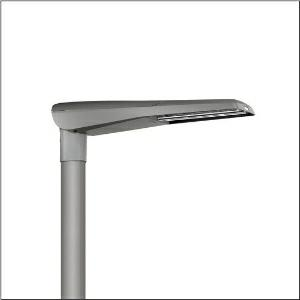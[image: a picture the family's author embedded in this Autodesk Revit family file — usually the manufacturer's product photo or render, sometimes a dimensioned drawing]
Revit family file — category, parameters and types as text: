
# Revit family: streetlight_sl_11_iq_mini___st0_5st0_5_5xc2hc1f08he_bd04
name_source: partatom
category: Lighting Fixtures
units: mm (PartAtom-declared; Revit-internal decimal feet)

## family parameters
Cut with Voids When Loaded = No
Host = Face
Light Source = No
Part Type = Normal
Room Calculation Point = No
Round Connector Dimension = Use Diameter
Shared = No

## types (1)
- --- (1 x LED, 6780 lm, 63.6 W, 2200K)
    Apparent Load = 64 VA
    CIE Flux Codes = 43 74 97 100 100
    Color Rendering = 70
    Color Temperature = 2200K
    Default Elevation = 1800 mm
    Description = Streetlight SL 11 iQ mini, mast luminaire, primary light control with 3 zone facetted reflector, of plastic, silver coated, highly specular, primary optical cover: cover, of PMMA, transparent, light distribution: ST0.5ST0.5, light emission: direct distribution, primary light characteristic: asymmetric, installation type: post-top, side-entry, lamps: LED, High Power LED, rated values: 8.280lm | 62,2W | 133,1lm/W (begin service life); end service life: 8.280lm | 65,6W; at 50% lumin. flux: 4.140lm | 29,4W | 140,8lm/W, colour temperature: 2200/2700/3000/4000K, colour rendering: CRI > 70, light colour: 722/727/730/740, light setting 1 begin service life: 100% | 8.280lm | 62,2W | 133,1lm/W | 3.000K, light setting 1 end service life: 65,6W, further light settings possible, control: Street-Remote, Auto-Match, Temp-Guard, Lumen-Switch, Night-Set, Smart-Wire, Light-Fading, Desk-Remote (wireless, voltage-free reading and setting of iQ features in the workshop via application-optimized NFC function/RFID function), optimised constant luminous flux control (CLO 2.0), with cable H07RN-F 3x 1.5mm², mains connection: 230..240V, AC, 50/60Hz, connection cable pre-assembled, cable length: 8,5m, luminaire housing, of diecast aluminium, powder-coated, SITECO metallic grey (DB 702S), please order mast flange separately, inclination adjustable without tools: 0°, 5°, 10°, 15° (post-top) | 0°, -5°, -10°, -15° (side-entry), sealing non-destructively replaceable, multi-level sealing system, length: 736mm, width: 174mm, height: 116mm, mast flange for spigot size: 42mm (side-entry): 5XC10008XM4, 60/48mm (side-entry/post-top): 5XC10108XM2, 76/60mm (side-entry/post-top): 5XC10108XM1, equipment: Power, protection rating (complete): IP66, insulation class (complete): insulation class II (safety insulation), certification: CE, ENEC, ENEC+, VDE, impact resistance: IK10, permissible operating ambient temperature for outdoor applications: -25..+50°C, standard-compliant lighting for roads and squares, Environmental Product Declaration (EPD) tested and certified by an independent institute, packaging unit: 1 piece

Light Distribution: ST0.5ST0.5
    Height = 116 mm
    Lamp = 1 x LED
    Lamp Light Flux = 6780 lm
    Lamp Power = 63.6 W
    Lamp count = 1
    Length = 736 mm
    Luminous efficacy = 107 lm/W
    Manufacturer = Siteco
    ModVariant = No
    Model = 5XC2HC1F08HE
    Number of Poles = 1
    OnlyDefault = Yes
    Power Factor = 1
    Product Name = Streetlight SL 11 iQ mini | ST0.5ST0.5
    Product group = mast luminaire | pylon top
    ProductGroupID = 6100
    Protection Class = Protection class II
    Protection Degree = IP 66
    RLX_Detail_Level = 1
    RLX_Emergency_Light_Flux = 0 lm
    RLX_Emergency_Type = 0
    RLX_Emergency_Type_DB = No
    RlxData = <blob elided: 58573 chars, md5=ace7585c>
    Socket = socket
    Standby Power = 0 W
    System Light Flux = 6780 lm
    System Power = 64 W
    Type Comments = individual setting: luminous flux: 100 % | dim-lin: 254 | 866 mA
    Type Image = l_1003508.jpg
    URL = http://relux.com
    VarID = @adj_042569
    Voltage = 0 V
    Weight = 0.00 kg
    Width = 174 mm

## geometry (parser evidence)
native form markers: Blend x4, Sweep x13
no freeform markers — native parametric forms only
